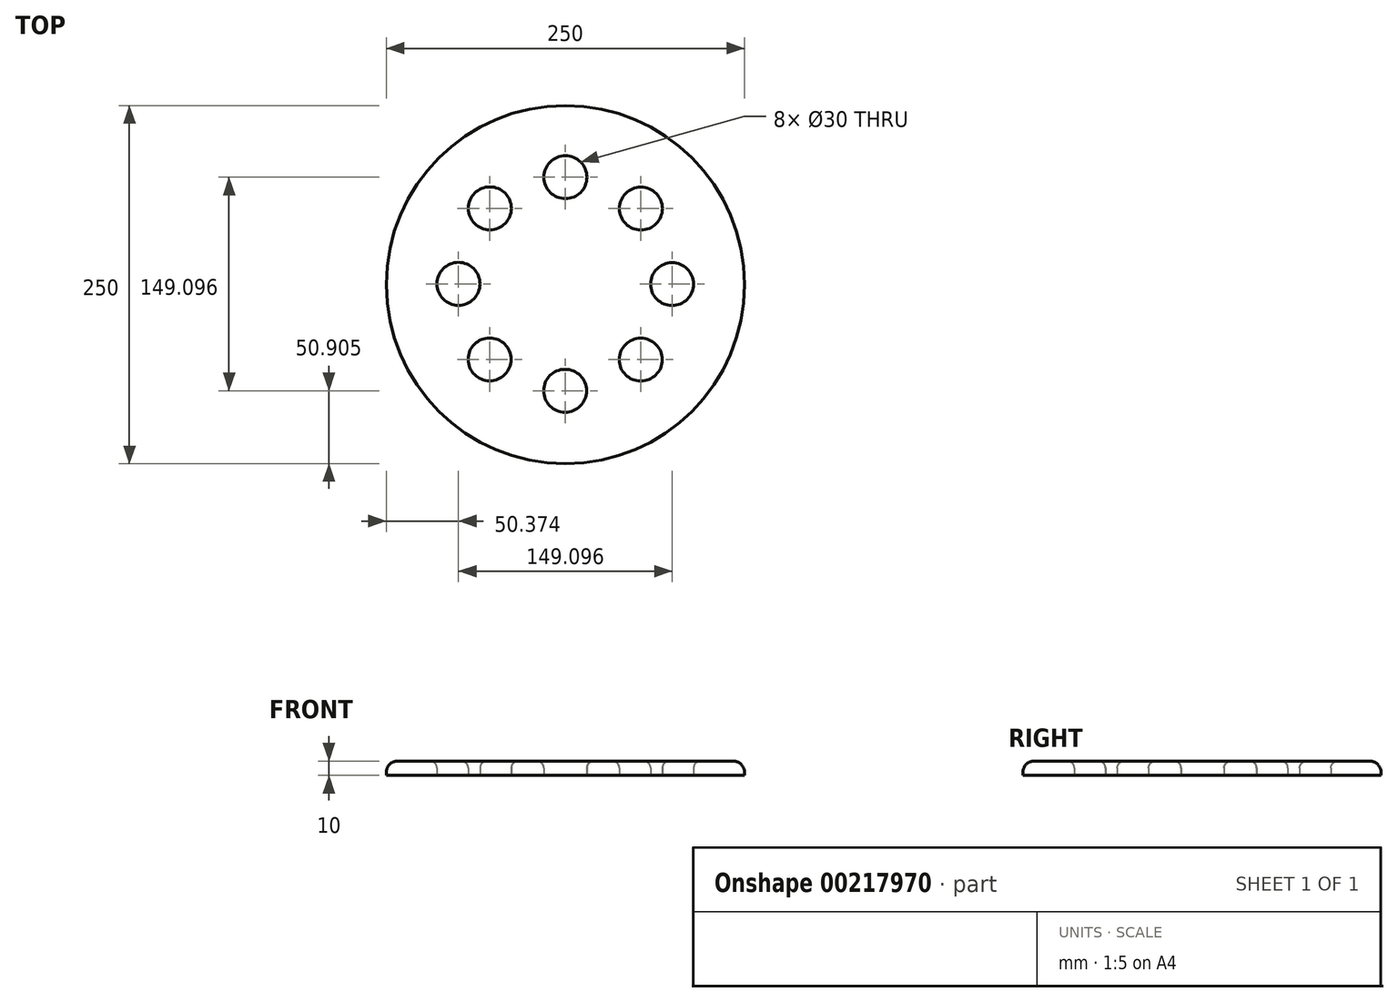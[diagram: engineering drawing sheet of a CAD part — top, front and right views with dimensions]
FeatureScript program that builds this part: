
annotation { "Feature Type Name" : "Feature", "Feature Type Description" : "" }
export const myFeature = defineFeature(function(context is Context, id is Id, definition is map)
    precondition{}
    {
        {
            var Q0;
            Q0=qCreatedBy(makeId("Top.planeOp"),FACE);
            var sketch = newSketch(context, id + "F0", { "sketchPlane" : qUnion([Q0])});
            skCircle(sketch, "E0", {"center": v(0, 30.95) * mm, "radius": 125 * mm});
            skSolve(sketch);
        }
        {
            var Q0;
            Q0=makeQuery(id+"F0.imprint","IMPRINT",FACE,{"disambiguationData":[TD([[makeQuery(id+"F0.imprint","IMPRINT",EDGE,{"derivedFrom":sQuery(id+"F0.wireOp",EDGE,"E0")}),1.0]])]});
            var sketch = newSketch(context, id + "F1", { "sketchPlane" : qUnion([Q0])});
            skCircle(sketch, "E1", {"center": v(0, 105.95) * mm, "radius": 15 * mm});
            skCircle(sketch, "E2.1.0", {"center": v(-52.74, 84.17) * mm, "radius": 15 * mm});
            skCircle(sketch, "E2.2.0", {"center": v(-74.63, 31.48) * mm, "radius": 15 * mm});
            skCircle(sketch, "E2.3.0", {"center": v(-52.85, -21.26) * mm, "radius": 15 * mm});
            skCircle(sketch, "E2.4.0", {"center": v(-0.16, -43.15) * mm, "radius": 15 * mm});
            skCircle(sketch, "E2.5.0", {"center": v(52.58, -21.37) * mm, "radius": 15 * mm});
            skCircle(sketch, "E2.6.0", {"center": v(74.47, 31.32) * mm, "radius": 15 * mm});
            skCircle(sketch, "E2.7.0", {"center": v(52.7, 84.06) * mm, "radius": 15 * mm});
            skPoint(sketch, "E2.center", {"position": v(-0.08, 31.4) * mm});
            skSolve(sketch);
        }
        {
            var Q0;
            Q0=makeQuery(id+"F1.imprint","IMPRINT",FACE,{"disambiguationData":[TD([[makeQuery(id+"F1.imprint","IMPRINT",EDGE,{"derivedFrom":sQuery(id+"F1.wireOp",EDGE,"E1")}),-1.0]])]});
            extrude(context, id + "F2", {"entities" : qUnion([Q0]), "depth" : 10 * mm});
        }
        {
            var Q0;
            Q0=makeQuery(id+"F2.opExtrude","CAP_EDGE",EDGE,{"disambiguationData":[OSD([sQuery(id+"F0.wireOp",EDGE,"E0")])],"isStart":false});
            fillet(context, id + "F3", {"entities" : qUnion([Q0]), "radius" : 8 * mm, "tangentPropagation" : true, "allowEdgeOverflow" : false});
        }
        {
            var Q0;
            Q0=makeQuery(id+"F2.opExtrude","CAP_EDGE",EDGE,{"disambiguationData":[OSD([sQuery(id+"F1.wireOp",EDGE,"E2.6.0")])],"isStart":false});
            var Q1;
            Q1=makeQuery(id+"F2.opExtrude","CAP_EDGE",EDGE,{"disambiguationData":[OSD([sQuery(id+"F1.wireOp",EDGE,"E2.5.0")])],"isStart":false});
            var Q2;
            Q2=makeQuery(id+"F2.opExtrude","CAP_EDGE",EDGE,{"disambiguationData":[OSD([sQuery(id+"F1.wireOp",EDGE,"E2.4.0")])],"isStart":false});
            var Q3;
            Q3=makeQuery(id+"F2.opExtrude","CAP_EDGE",EDGE,{"disambiguationData":[OSD([sQuery(id+"F1.wireOp",EDGE,"E2.3.0")])],"isStart":false});
            var Q4;
            Q4=makeQuery(id+"F2.opExtrude","CAP_EDGE",EDGE,{"disambiguationData":[OSD([sQuery(id+"F1.wireOp",EDGE,"E2.2.0")])],"isStart":false});
            var Q5;
            Q5=makeQuery(id+"F2.opExtrude","CAP_EDGE",EDGE,{"disambiguationData":[OSD([sQuery(id+"F1.wireOp",EDGE,"E2.1.0")])],"isStart":false});
            var Q6;
            Q6=makeQuery(id+"F2.opExtrude","CAP_EDGE",EDGE,{"disambiguationData":[OSD([sQuery(id+"F1.wireOp",EDGE,"E1")])],"isStart":false});
            var Q7;
            Q7=makeQuery(id+"F2.opExtrude","CAP_EDGE",EDGE,{"disambiguationData":[OSD([sQuery(id+"F1.wireOp",EDGE,"E2.7.0")])],"isStart":false});
            fillet(context, id + "F4", {"entities" : qUnion([Q0, Q1, Q2, Q3, Q4, Q5, Q6, Q7]), "radius" : 5 * mm, "tangentPropagation" : true, "allowEdgeOverflow" : false});
        }
    });
